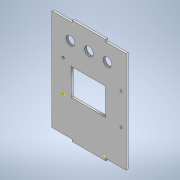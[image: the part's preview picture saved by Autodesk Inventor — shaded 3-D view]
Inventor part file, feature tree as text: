
AUTODESK INVENTOR PART (.ipt)
format: ipt  version: 2020 (Build 240168000, 168)  size: 147,968 bytes
history: native  units: in
note: dims shown in document units (in); Inventor stores cm internally (conversion verified against a paired STEP export)
features: sketch x4, extrude x3
ambient origin geometry x8: Origin, YZ Plane, XZ Plane, XY Plane, X Axis, Y Axis, Z Axis, Center Point
bodies: Solid1 (feature_tree)
feature tree (7):
  extrude  "Extrusion1"  Depth=0.1181in
  extrude  "Extrusion2"  Depth=1.9685in
  sketch  "Sketch3"  dims[d4=1.9685in d5=1.1811in]
  extrude  "Extrusion3"  Depth=1.1811in
  sketch  "Sketch1"  dims[d0=5.9055in d1=0.1181in]
  sketch  "Sketch2"  dims[d2=0.1181in d3=1.9685in]
  sketch  "Sketch4"  dims[d6=1.1811in d7=0.1181in d8=0.0in d40=0.1181in d41=0.0in d48=0.5118in d49=0.5118in d50=0.5118in d52=0.1181in d53=0.0in d9=0.0197in d10=0.0344in]
